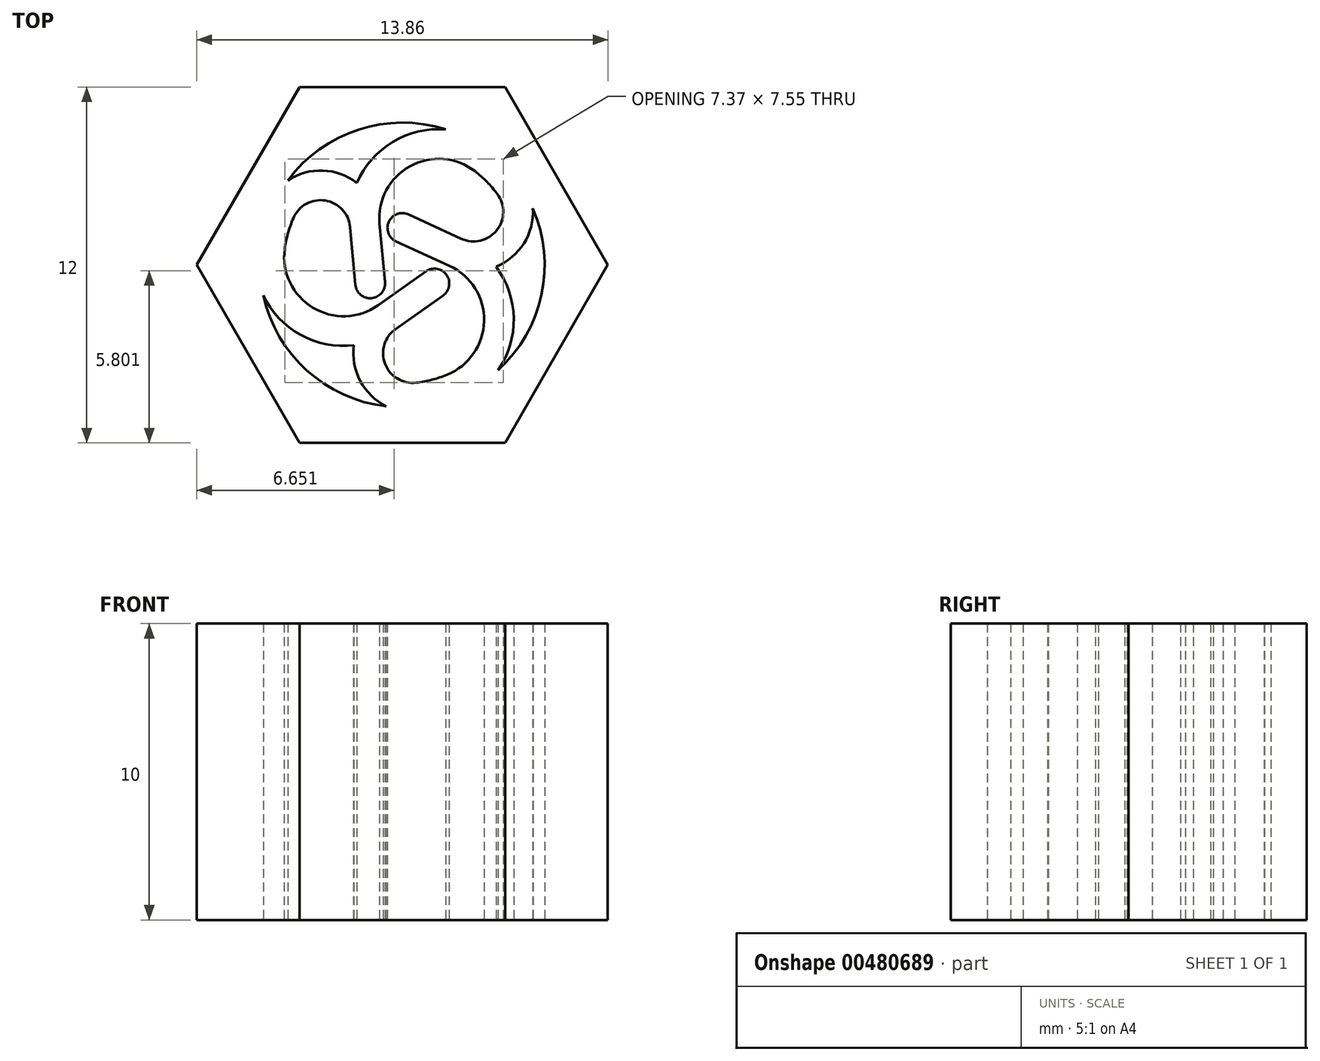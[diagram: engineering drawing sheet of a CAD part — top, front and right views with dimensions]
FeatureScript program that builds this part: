
annotation { "Feature Type Name" : "Feature", "Feature Type Description" : "" }
export const myFeature = defineFeature(function(context is Context, id is Id, definition is map)
    precondition{}
    {
        {
            var Q0;
            Q0=qCreatedBy(makeId("Top.planeOp"),FACE);
            var sketch = newSketch(context, id + "F0", { "sketchPlane" : qUnion([Q0])});
            skCircle(sketch, "E0", {"center": v(0, 0) * mm, "radius": 0.75 * mm, "construction": true});
            skCircle(sketch, "E1", {"center": v(0, 0) * mm, "radius": 1.75 * mm, "construction": true});
            skLineSegment(sketch, "E2", {"start": v(0, 0.75) * mm, "end": v(0, 1.75) * mm, "construction": true});
            skPoint(sketch, "E3", {"position": v(0, 1.25) * mm});
            skArc(sketch, "E4", {"start": v(0.2, 1.7) * mm, "mid": v(-0.49, 1.36) * mm, "end": v(0, 0.75) * mm});
            skArc(sketch, "E5", {"start": v(-3.67, 1.58) * mm, "mid": v(-3.85, 1.07) * mm, "end": v(-3.96, 0.54) * mm});
            skLineSegment(sketch, "E6", {"start": v(0, 0) * mm, "end": v(-1.6, 3.67) * mm, "construction": true});
            skLineSegment(sketch, "E7", {"start": v(0, 0) * mm, "end": v(3.97, -0.45) * mm, "construction": true});
            skArc(sketch, "E8", {"start": v(1.37, -1.03) * mm, "mid": v(1.42, -0.26) * mm, "end": v(0.65, -0.37) * mm});
            skPoint(sketch, "E9", {"position": v(1.52, -0.87) * mm});
            skCircle(sketch, "E10", {"center": v(1.08, -0.62) * mm, "radius": 0.75 * mm, "construction": true});
            skLineSegment(sketch, "E11", {"start": v(1.6, -0.03) * mm, "end": v(-0.2, 0.8) * mm});
            skLineSegment(sketch, "E12", {"start": v(1.99, 0.89) * mm, "end": v(0.2, 1.7) * mm});
            skLineSegment(sketch, "E13", {"start": v(0, 0) * mm, "end": v(-2.37, -3.22) * mm, "construction": true});
            skArc(sketch, "E14", {"start": v(-1.58, -0.67) * mm, "mid": v(-0.93, -1.1) * mm, "end": v(-0.65, -0.37) * mm});
            skCircle(sketch, "E15", {"center": v(-1.08, -0.62) * mm, "radius": 0.75 * mm, "construction": true});
            skCircle(sketch, "E16", {"center": v(0, 1.25) * mm, "radius": 0.75 * mm, "construction": true});
            skLineSegment(sketch, "E17", {"start": v(-0.23, -2.16) * mm, "end": v(1.37, -1.03) * mm});
            skLineSegment(sketch, "E18", {"start": v(-0.83, -1.36) * mm, "end": v(0.8, -0.22) * mm});
            skLineSegment(sketch, "E19", {"start": v(-1.76, 1.28) * mm, "end": v(-1.58, -0.67) * mm});
            skLineSegment(sketch, "E20", {"start": v(-0.77, 1.4) * mm, "end": v(-0.58, -0.58) * mm});
            skCircle(sketch, "E21.cCircle", {"center": v(0, 0) * mm, "radius": 6 * mm, "construction": true});
            skLineSegment(sketch, "E21.0", {"start": v(-3.46, 6) * mm, "end": v(3.46, 6) * mm});
            skLineSegment(sketch, "E21.1", {"start": v(3.46, 6) * mm, "end": v(6.93, 0) * mm});
            skLineSegment(sketch, "E21.2", {"start": v(6.93, 0) * mm, "end": v(3.46, -6) * mm});
            skLineSegment(sketch, "E21.3", {"start": v(3.46, -6) * mm, "end": v(-3.46, -6) * mm});
            skLineSegment(sketch, "E21.4", {"start": v(-3.46, -6) * mm, "end": v(-6.93, 0) * mm});
            skLineSegment(sketch, "E21.5", {"start": v(-6.93, 0) * mm, "end": v(-3.46, 6) * mm});
            skPoint(sketch, "E21.0.midPoint", {"position": v(0, 6) * mm});
            skArc(sketch, "E22.trimOffspring", {"start": v(0.47, -3.97) * mm, "mid": v(1, -3.87) * mm, "end": v(1.51, -3.7) * mm});
            skArc(sketch, "E23.trimOffspring", {"start": v(3.2, 2.4) * mm, "mid": v(2.85, 2.8) * mm, "end": v(2.45, 3.16) * mm});
            skPoint(sketch, "E24.visualSharp", {"position": v(-1, 3.87) * mm});
            skArc(sketch, "E24.filletArc", {"start": v(2.45, 3.16) * mm, "mid": v(0.26, 3.33) * mm, "end": v(-0.77, 1.4) * mm});
            skPoint(sketch, "E25.visualSharp", {"position": v(-1.96, 3.49) * mm});
            skArc(sketch, "E25.filletArc", {"start": v(-1.76, 1.28) * mm, "mid": v(-2.6, 2.17) * mm, "end": v(-3.67, 1.58) * mm});
            skArc(sketch, "E26", {"start": v(-4.7, -1.02) * mm, "mid": v(-3.22, -3.56) * mm, "end": v(-0.54, -4.77) * mm});
            skPoint(sketch, "E27.visualSharp", {"position": v(-2.04, -3.44) * mm});
            skArc(sketch, "E27.filletArc", {"start": v(-0.23, -2.16) * mm, "mid": v(-0.58, -3.34) * mm, "end": v(0.47, -3.97) * mm});
            skPoint(sketch, "E28.visualSharp", {"position": v(4, -0.04) * mm});
            skArc(sketch, "E28.filletArc", {"start": v(1.99, 0.89) * mm, "mid": v(3.18, 1.16) * mm, "end": v(3.2, 2.4) * mm});
            skPoint(sketch, "E29.visualSharp", {"position": v(3.85, -1.08) * mm});
            skArc(sketch, "E29.filletArc", {"start": v(1.51, -3.7) * mm, "mid": v(2.76, -1.9) * mm, "end": v(1.6, -0.03) * mm});
            skPoint(sketch, "E30.visualSharp", {"position": v(-2.86, -2.8) * mm});
            skArc(sketch, "E30.filletArc", {"start": v(-3.96, 0.54) * mm, "mid": v(-3.02, -1.44) * mm, "end": v(-0.83, -1.36) * mm});
            skArc(sketch, "E31", {"start": v(-0.77, 1.4) * mm, "mid": v(-0.78, 1.48) * mm, "end": v(-0.8, 1.56) * mm});
            skArc(sketch, "E32", {"start": v(1.46, 4.57) * mm, "mid": v(-0.32, 4.15) * mm, "end": v(-1.53, 2.77) * mm});
            skArc(sketch, "E33.trimOffspring", {"start": v(-1.53, 2.77) * mm, "mid": v(-2.68, 3.18) * mm, "end": v(-3.86, 2.85) * mm});
            skArc(sketch, "E34", {"start": v(-0.23, -2.16) * mm, "mid": v(-0.23, -2.17) * mm, "end": v(-0.24, -2.17) * mm});
            skArc(sketch, "E35", {"start": v(1.99, 0.89) * mm, "mid": v(2, 0.88) * mm, "end": v(2, 0.88) * mm});
            skArc(sketch, "E36", {"start": v(1.6, -0.03) * mm, "mid": v(1.67, -0.07) * mm, "end": v(1.75, -0.1) * mm});
            skArc(sketch, "E37.trimOffspring", {"start": v(3.16, -0.06) * mm, "mid": v(3.76, -1.8) * mm, "end": v(3.23, -3.55) * mm});
            skArc(sketch, "E38.trimOffspring", {"start": v(3.16, -0.06) * mm, "mid": v(4.1, 0.73) * mm, "end": v(4.4, 1.92) * mm});
            skArc(sketch, "E39.trimOffspring", {"start": v(1.46, 4.57) * mm, "mid": v(-1.47, 4.57) * mm, "end": v(-3.86, 2.85) * mm});
            skArc(sketch, "E40.trimOffspring", {"start": v(3.23, -3.55) * mm, "mid": v(4.7, -1) * mm, "end": v(4.4, 1.92) * mm});
            skArc(sketch, "E41", {"start": v(-0.83, -1.36) * mm, "mid": v(-0.9, -1.41) * mm, "end": v(-0.96, -1.47) * mm});
            skArc(sketch, "E42", {"start": v(-1.63, -2.7) * mm, "mid": v(-3.43, -2.36) * mm, "end": v(-4.7, -1.02) * mm});
            skArc(sketch, "E43.trimOffspring", {"start": v(-1.63, -2.7) * mm, "mid": v(-1.42, -3.91) * mm, "end": v(-0.54, -4.77) * mm});
            skSolve(sketch);
        }
        {
            var Q0;
            Q0=makeQuery(id+"F0.imprint","IMPRINT",FACE,{"disambiguationData":[TD([[makeQuery(id+"F0.imprint","IMPRINT",EDGE,{"derivedFrom":sQuery(id+"F0.wireOp",EDGE,"E5")}),-1.0]])]});
            extrude(context, id + "F1", {"entities" : qUnion([Q0]), "depth" : 10 * mm});
        }
    });
